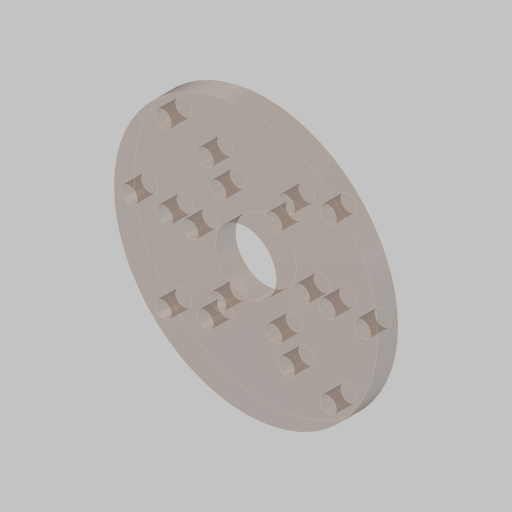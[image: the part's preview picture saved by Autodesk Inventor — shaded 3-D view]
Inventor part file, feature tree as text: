
AUTODESK INVENTOR PART (.ipt)
format: ipt  version: 2023.5 (Build 275446000, 446)  size: 163,840 bytes
history: native  units: in
note: dims shown in document units (in); Inventor stores cm internally (conversion verified against a paired STEP export)
features: sketch x1, extrude x1, hole x1
ambient origin geometry x8: Origin, YZ Plane, XZ Plane, XY Plane, X Axis, Y Axis, Z Axis, Center Point
bodies: Solid1 (feature_tree)
feature tree (3):
  sketch  "Sketch1"  dims[d0=0.75in d1=2.5in d2=0.375in d3=1.375in d8=0.25in d9=0.0in d18=2.0in d19=2.3622in d21=360.0deg d23=0.201in d24=0.75in d25=0.385in d26=0.25in d27=0.5635in d28=1.0in d29=0.8108in d30=45.0deg d31=1.5748in d33=360.0deg d35=1.5748in d37=360.0deg]
  extrude  "Extrusion1"  Depth=0.25in
  hole  "Hole2"  [1 undecoded]
note: 1 required parameter value undecoded (feature->parameter linkage not recoverable at this tier; creation-order binding heuristic only, values carry confidence <= 0.55)
